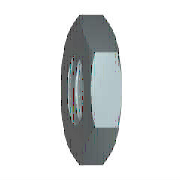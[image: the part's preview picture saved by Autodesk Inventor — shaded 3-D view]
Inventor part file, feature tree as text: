
AUTODESK INVENTOR PART (.ipt)
format: ipt  version: 2022 (Build 260153000, 153)  size: 165,888 bytes
history: native  units: mm (DEFAULTED — no unit token found)
features: sketch x3, extrude x1, chamfer x1, hole x1, other x1, plane x1
ambient origin geometry x7: Origin, YZ Plane, XZ Plane, X Axis, Y Axis, Z Axis, Center Point
bodies: Solid1 (feature_tree)
feature tree (8):
  extrude  "Cuerpo"  Depth=2.2mm
  chamfer  "Chaflán1"  Angle=30.0deg  [1 undecoded]
  hole  "Rosca"  [1 undecoded]
  other  "Work Axis1"
  plane  "Work Plane1"
  sketch  "Boceto1"  dims[d0=8.082904mm d1=2.2mm]
  sketch  "Boceto2"  dims[d2=0.0mm]
  sketch  "Boceto3"  dims[d3=30.0deg d4=30.0deg d5=5.9mm d6=5.9mm d7=90.0deg d25=3.242mm d26=6.0mm d27=4.0mm d28=2.0mm d29=14.3117mm d30=8.0mm d31=20.594885mm d8=0.378886mm d9=30.0deg d10=0.378886mm d11=30.0deg d13=0.0mm d14=0.0mm d39=0.0mm d40=0.378886mm d41=0.378886mm d42=0.0mm]
note: 2 required parameter values undecoded (feature->parameter linkage not recoverable at this tier; creation-order binding heuristic only, values carry confidence <= 0.55)
